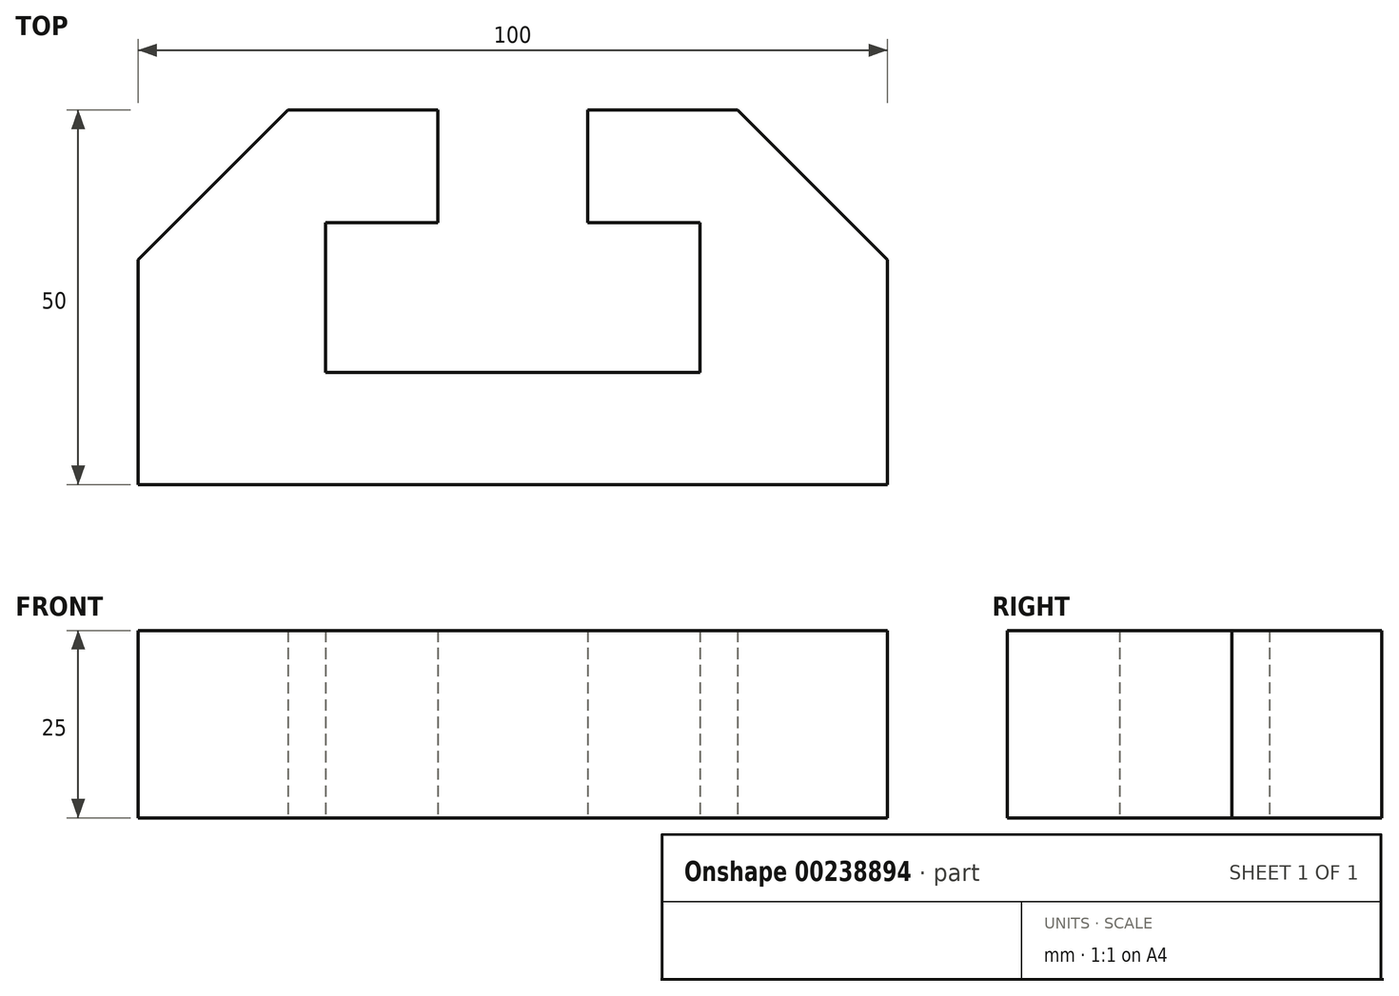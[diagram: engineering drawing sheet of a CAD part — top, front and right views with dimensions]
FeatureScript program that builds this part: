
annotation { "Feature Type Name" : "Feature", "Feature Type Description" : "" }
export const myFeature = defineFeature(function(context is Context, id is Id, definition is map)
    precondition{}
    {
        {
            var Q0;
            Q0=qCreatedBy(makeId("Top.planeOp"),FACE);
            var sketch = newSketch(context, id + "F0", { "sketchPlane" : qUnion([Q0])});
            skLineSegment(sketch, "E0", {"start": v(-52.82, -52.78) * mm, "end": v(47.18, -52.78) * mm});
            skLineSegment(sketch, "E1", {"start": v(-52.82, -52.78) * mm, "end": v(-52.82, -22.78) * mm});
            skLineSegment(sketch, "E2", {"start": v(47.18, -52.78) * mm, "end": v(47.18, -22.78) * mm});
            skLineSegment(sketch, "E3", {"start": v(-32.82, -2.78) * mm, "end": v(-12.82, -2.78) * mm});
            skLineSegment(sketch, "E4", {"start": v(27.18, -2.78) * mm, "end": v(7.18, -2.78) * mm});
            skLineSegment(sketch, "E5", {"start": v(7.18, -2.78) * mm, "end": v(7.18, -17.78) * mm});
            skLineSegment(sketch, "E6", {"start": v(-12.82, -2.78) * mm, "end": v(-12.82, -17.78) * mm});
            skLineSegment(sketch, "E7", {"start": v(7.18, -17.78) * mm, "end": v(22.18, -17.78) * mm});
            skLineSegment(sketch, "E8", {"start": v(-12.82, -17.78) * mm, "end": v(-27.82, -17.78) * mm});
            skLineSegment(sketch, "E9", {"start": v(-27.82, -17.78) * mm, "end": v(-27.82, -37.78) * mm});
            skLineSegment(sketch, "E10", {"start": v(22.18, -17.78) * mm, "end": v(22.18, -37.78) * mm});
            skLineSegment(sketch, "E11", {"start": v(-27.82, -37.78) * mm, "end": v(22.18, -37.78) * mm});
            skLineSegment(sketch, "E12", {"start": v(27.18, -2.78) * mm, "end": v(47.18, -22.78) * mm});
            skLineSegment(sketch, "E13", {"start": v(-32.82, -2.78) * mm, "end": v(-52.82, -22.78) * mm});
            skSolve(sketch);
        }
        {
            var Q0;
            Q0 = qSketchRegion(id + "F0", true);
            extrude(context, id + "F1", {"entities" : qUnion([Q0]), "depth" : 25 * mm});
        }
    });
